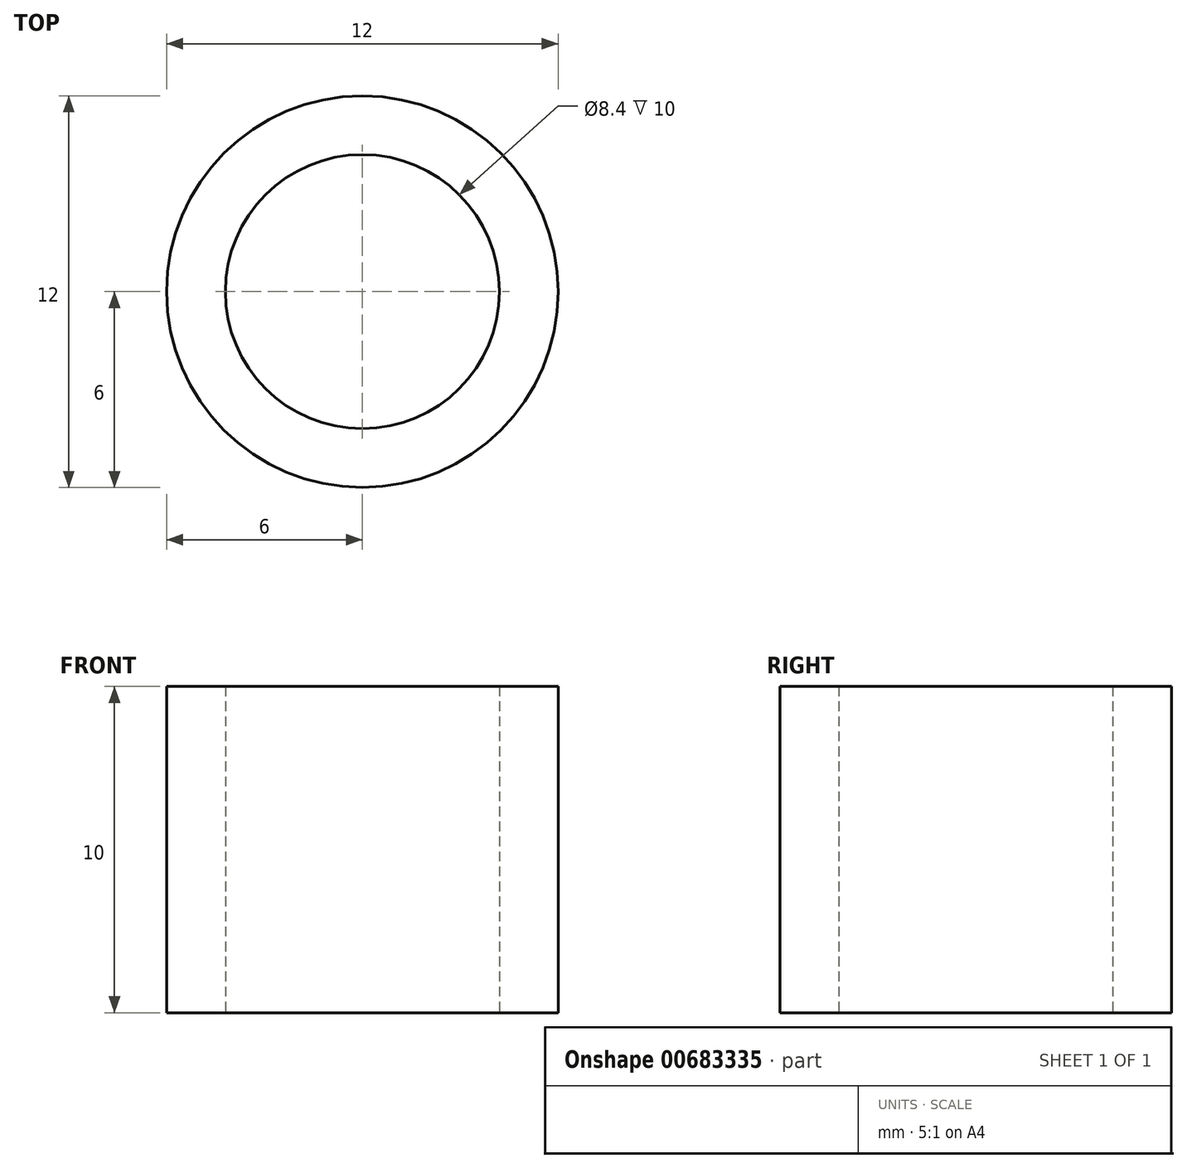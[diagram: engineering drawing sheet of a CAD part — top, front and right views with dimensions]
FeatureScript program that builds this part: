
annotation { "Feature Type Name" : "Feature", "Feature Type Description" : "" }
export const myFeature = defineFeature(function(context is Context, id is Id, definition is map)
    precondition{}
    {
        {
            var Q0;
            Q0=qCreatedBy(makeId("Top.planeOp"),FACE);
            var sketch = newSketch(context, id + "F0", { "sketchPlane" : qUnion([Q0])});
            skCircle(sketch, "E0", {"center": v(0, 0) * mm, "radius": 6 * mm});
            skCircle(sketch, "E1", {"center": v(0, 0) * mm, "radius": 4.2 * mm});
            skSolve(sketch);
        }
        {
            var Q0;
            Q0 = qSketchRegion(id + "F0", true);
            extrude(context, id + "F1", {"entities" : qUnion([Q0]), "depth" : 10 * mm, "offsetDistance" : 25 * mm});
        }
    });
